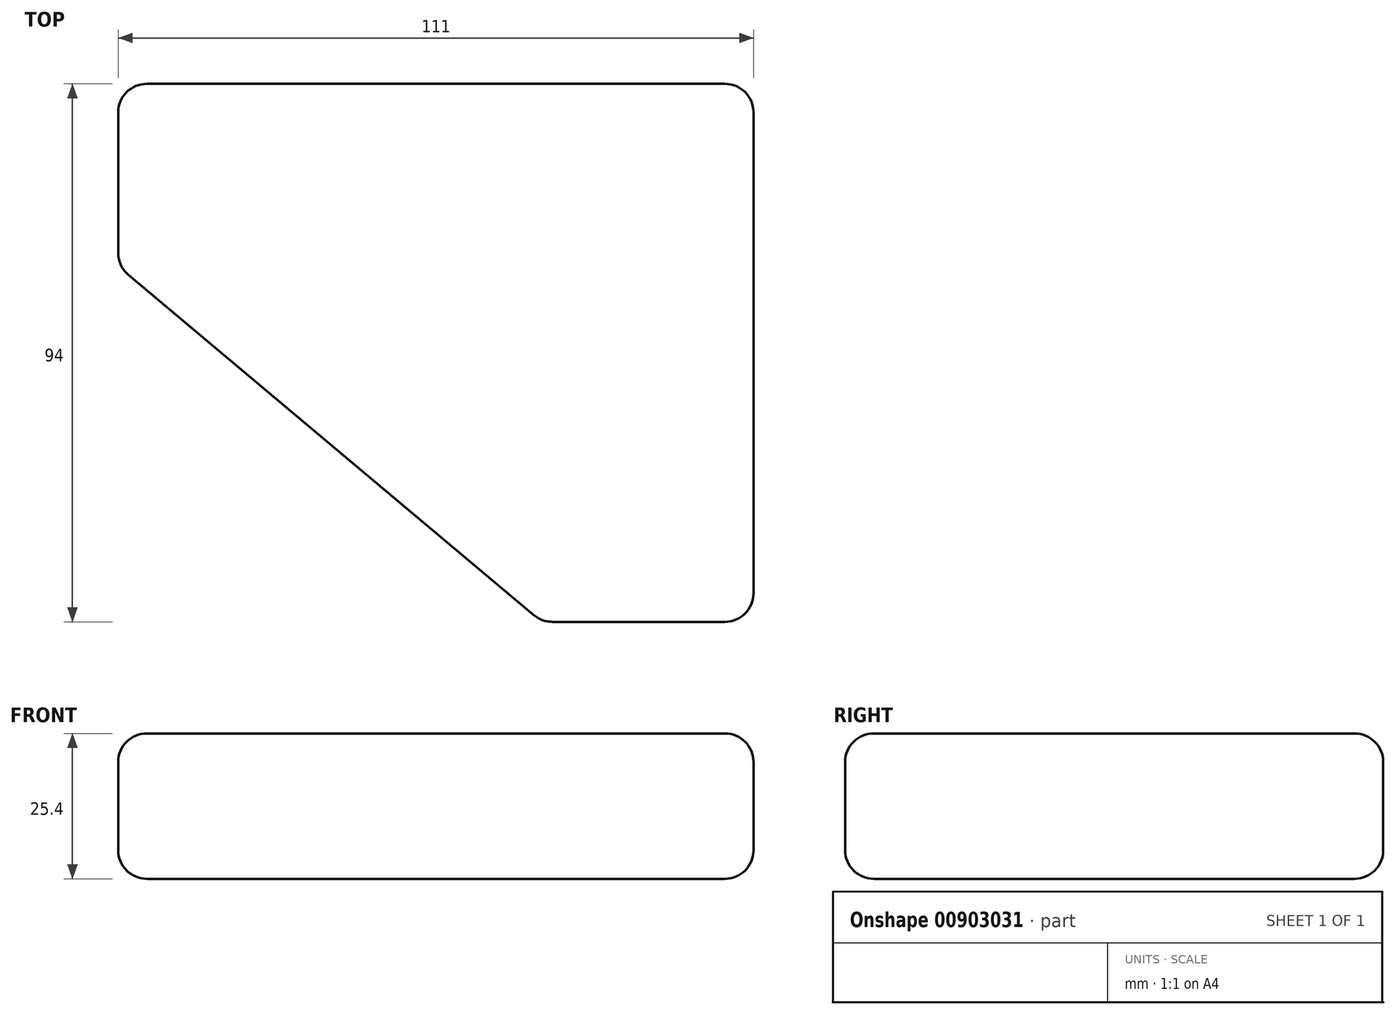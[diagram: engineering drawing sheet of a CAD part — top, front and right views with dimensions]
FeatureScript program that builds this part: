
annotation { "Feature Type Name" : "Feature", "Feature Type Description" : "" }
export const myFeature = defineFeature(function(context is Context, id is Id, definition is map)
    precondition{}
    {
        {
            var Q0;
            Q0=qCreatedBy(makeId("Top.planeOp"),FACE);
            var sketch = newSketch(context, id + "F0", { "sketchPlane" : qUnion([Q0])});
            skLineSegment(sketch, "E0.bottom", {"start": v(-56, 50) * mm, "end": v(55, 50) * mm});
            skLineSegment(sketch, "E0.top", {"start": v(18, -44) * mm, "end": v(55, -44) * mm});
            skLineSegment(sketch, "E0.left", {"start": v(-56, 50) * mm, "end": v(-56, 18.1) * mm});
            skLineSegment(sketch, "E0.right", {"start": v(55, 50) * mm, "end": v(55, -44) * mm});
            skLineSegment(sketch, "E1", {"start": v(-56, 18.1) * mm, "end": v(18, -44) * mm});
            skSolve(sketch);
        }
        {
            var Q0;
            Q0=makeQuery(id+"F0.imprint","IMPRINT",FACE,{"disambiguationData":[TD([[makeQuery(id+"F0.imprint","IMPRINT",EDGE,{"derivedFrom":sQuery(id+"F0.wireOp",EDGE,"E0.bottom")}),-1.0]])]});
            extrude(context, id + "F1", {"entities" : qUnion([Q0]), "depth" : 25.4 * mm, "offsetDistance" : 25.4 * mm});
        }
        {
            var Q0;
            Q0=makeQuery(id+"F1.opExtrude","CAP_FACE",FACE,{"disambiguationData":[OSD([sQuery(id+"F0.wireOp",EDGE,"E0.bottom"),sQuery(id+"F0.wireOp",EDGE,"E0.top"),sQuery(id+"F0.wireOp",EDGE,"E0.left"),sQuery(id+"F0.wireOp",EDGE,"E0.right"),sQuery(id+"F0.wireOp",EDGE,"E1")])],"isStart":true});
            var Q1;
            Q1=makeQuery(id+"F1.opExtrude","CAP_FACE",FACE,{"disambiguationData":[OSD([sQuery(id+"F0.wireOp",EDGE,"E0.bottom"),sQuery(id+"F0.wireOp",EDGE,"E0.top"),sQuery(id+"F0.wireOp",EDGE,"E0.left"),sQuery(id+"F0.wireOp",EDGE,"E0.right"),sQuery(id+"F0.wireOp",EDGE,"E1")])],"isStart":false});
            var Q2;
            Q2=makeQuery(id+"F1.opExtrude","SWEPT_EDGE",EDGE,{"disambiguationData":[OSD([sQuery(id+"F0.wireOp",EDGE,"E0.bottom"),sQuery(id+"F0.wireOp",EDGE,"E0.left")])]});
            var Q3;
            Q3=makeQuery(id+"F1.opExtrude","SWEPT_EDGE",EDGE,{"disambiguationData":[OSD([sQuery(id+"F0.wireOp",EDGE,"E0.bottom"),sQuery(id+"F0.wireOp",EDGE,"E0.right")])]});
            var Q4;
            Q4=makeQuery(id+"F1.opExtrude","SWEPT_EDGE",EDGE,{"disambiguationData":[OSD([sQuery(id+"F0.wireOp",EDGE,"E0.left"),sQuery(id+"F0.wireOp",EDGE,"E1")])]});
            var Q5;
            Q5=makeQuery(id+"F1.opExtrude","SWEPT_EDGE",EDGE,{"disambiguationData":[OSD([sQuery(id+"F0.wireOp",EDGE,"E0.top"),sQuery(id+"F0.wireOp",EDGE,"E1")])]});
            var Q6;
            Q6=makeQuery(id+"F1.opExtrude","SWEPT_EDGE",EDGE,{"disambiguationData":[OSD([sQuery(id+"F0.wireOp",EDGE,"E0.top"),sQuery(id+"F0.wireOp",EDGE,"E0.right")])]});
            fillet(context, id + "F2", {"entities" : qUnion([Q0, Q1, Q2, Q3, Q4, Q5, Q6]), "radius" : 5 * mm, "tangentPropagation" : true, "allowEdgeOverflow" : false});
        }
    });
